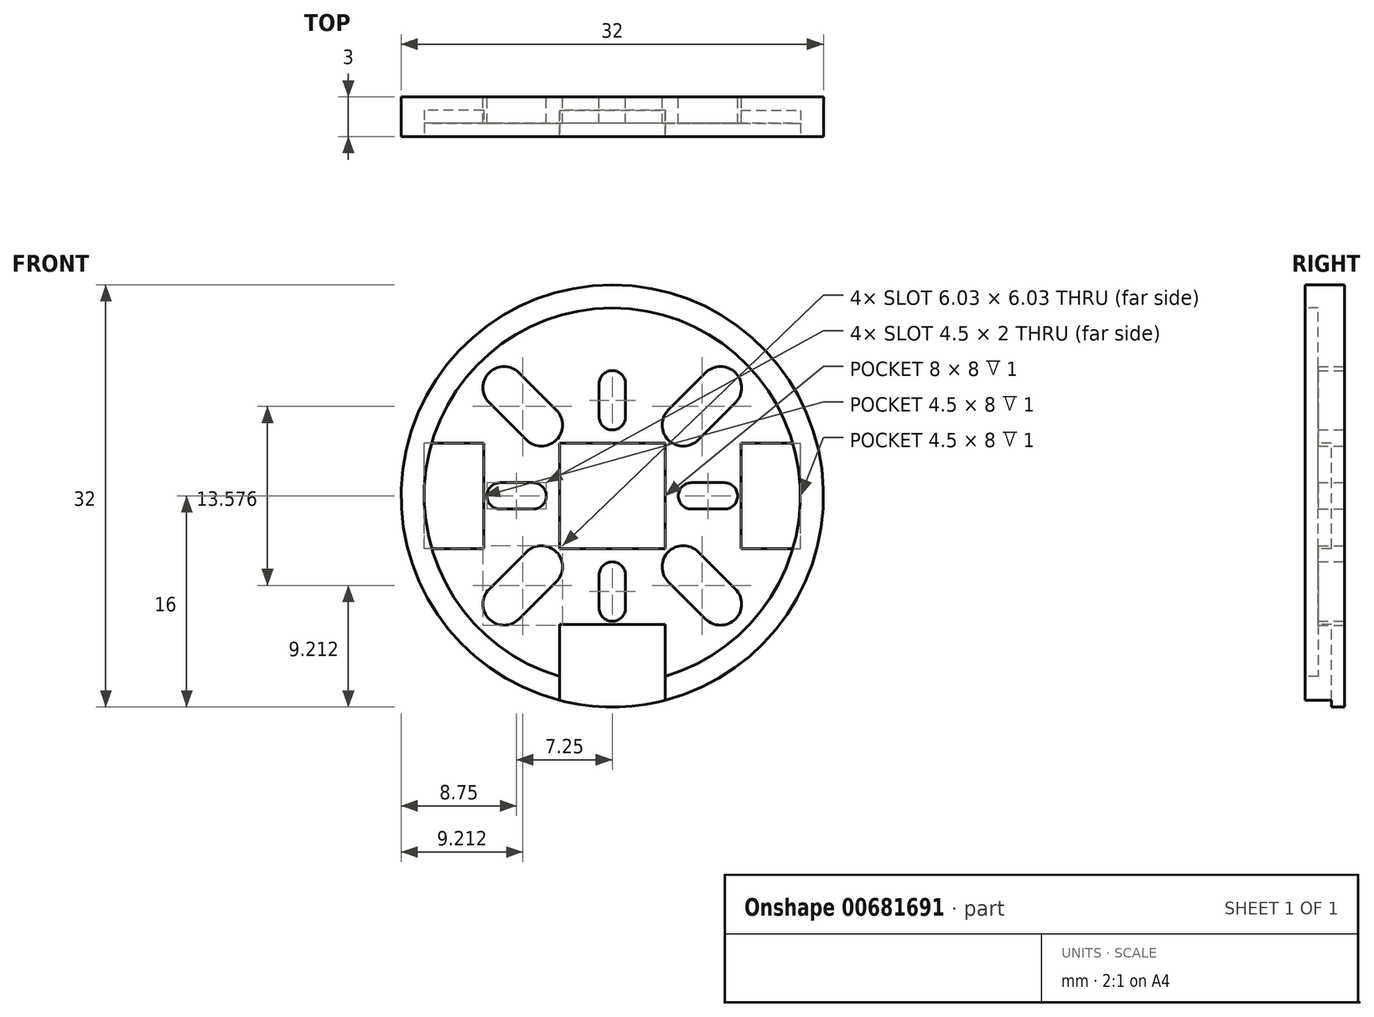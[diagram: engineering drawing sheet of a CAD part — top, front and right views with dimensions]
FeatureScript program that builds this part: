
annotation { "Feature Type Name" : "Feature", "Feature Type Description" : "" }
export const myFeature = defineFeature(function(context is Context, id is Id, definition is map)
    precondition{}
    {
        {
            var Q0;
            Q0=qCreatedBy(makeId("Front.planeOp"),FACE);
            var sketch = newSketch(context, id + "F0", { "sketchPlane" : qUnion([Q0])});
            skCircle(sketch, "E0", {"center": v(0, 0) * mm, "radius": 16 * mm});
            skSolve(sketch);
        }
        {
            var Q0;
            Q0 = qSketchRegion(id + "F0", true);
            extrude(context, id + "F1", {"entities" : qUnion([Q0]), "depth" : 3 * mm, "offsetDistance" : 25 * mm});
        }
        {
            var Q0;
            Q0=makeQuery(id+"F1.opExtrude","CAP_FACE",FACE,{"disambiguationData":[OSD([sQuery(id+"F0.wireOp",EDGE,"E0")])],"isStart":false});
            var sketch = newSketch(context, id + "F2", { "sketchPlane" : qUnion([Q0])});
            skArc(sketch, "E1", {"start": v(4, -13.68) * mm, "mid": v(0, 14.25) * mm, "end": v(-4, -13.68) * mm});
            skLineSegment(sketch, "E2.bottom", {"start": v(4, -16.68) * mm, "end": v(-4, -16.68) * mm});
            skLineSegment(sketch, "E2.left", {"start": v(4, -16.68) * mm, "end": v(4, -13.68) * mm});
            skLineSegment(sketch, "E2.right", {"start": v(-4, -16.68) * mm, "end": v(-4, -13.68) * mm});
            skPoint(sketch, "E2.middle", {"position": v(0, -15.18) * mm});
            skSolve(sketch);
        }
        {
            var Q0;
            Q0 = qSketchRegion(id + "F2", true);
            extrude(context, id + "F3", {"entities" : qUnion([Q0]), "operationType" : NewBodyOperationType.REMOVE, "oppositeDirection" : true, "depth" : 1 * mm, "offsetDistance" : 25 * mm});
        }
        {
            var Q0;
            Q0=makeQuery(id+"F3.boolean.opBoolean","COPY",FACE,{"derivedFrom":makeQuery(id+"F3.opExtrude","CAP_FACE",FACE,{"disambiguationData":[OSD([sQuery(id+"F2.wireOp",EDGE,"E1"),sQuery(id+"F2.wireOp",EDGE,"E2.bottom"),sQuery(id+"F2.wireOp",EDGE,"E2.left"),sQuery(id+"F2.wireOp",EDGE,"E2.right")])],"isStart":false})});
            var sketch = newSketch(context, id + "F4", { "sketchPlane" : qUnion([Q0])});
            skLineSegment(sketch, "E3.bottom", {"start": v(4, -4) * mm, "end": v(-4, -4) * mm});
            skLineSegment(sketch, "E3.top", {"start": v(4, 4) * mm, "end": v(-4, 4) * mm});
            skLineSegment(sketch, "E3.left", {"start": v(4, -4) * mm, "end": v(4, 4) * mm});
            skLineSegment(sketch, "E3.right", {"start": v(-4, -4) * mm, "end": v(-4, 4) * mm});
            skPoint(sketch, "E3.middle", {"position": v(0, 0) * mm});
            skLineSegment(sketch, "E4.bottom", {"start": v(-9.75, -4) * mm, "end": v(-14.25, -4) * mm});
            skLineSegment(sketch, "E4.top", {"start": v(-9.75, 4) * mm, "end": v(-14.25, 4) * mm});
            skLineSegment(sketch, "E4.left", {"start": v(-9.75, -4) * mm, "end": v(-9.75, 4) * mm});
            skLineSegment(sketch, "E4.right", {"start": v(-14.25, -4) * mm, "end": v(-14.25, 4) * mm});
            skPoint(sketch, "E4.middle", {"position": v(-12, 0) * mm});
            skLineSegment(sketch, "E5.MirrorCS", {"start": v(14.25, -4) * mm, "end": v(14.25, 4) * mm});
            skLineSegment(sketch, "E6.MirrorCS", {"start": v(9.75, -4) * mm, "end": v(14.25, -4) * mm});
            skLineSegment(sketch, "E7.MirrorCS", {"start": v(9.75, 4) * mm, "end": v(14.25, 4) * mm});
            skLineSegment(sketch, "E8.MirrorCS", {"start": v(9.75, -4) * mm, "end": v(9.75, 4) * mm});
            skLineSegment(sketch, "E9.1.0", {"start": v(4, -9.75) * mm, "end": v(-4, -9.75) * mm});
            skLineSegment(sketch, "E9.1.1", {"start": v(-4, -9.75) * mm, "end": v(-4, -14.25) * mm});
            skLineSegment(sketch, "E9.1.2", {"start": v(4, -14.25) * mm, "end": v(-4, -14.25) * mm, "construction": true});
            skLineSegment(sketch, "E9.1.3", {"start": v(4, -9.75) * mm, "end": v(4, -14.25) * mm});
            skLineSegment(sketch, "E9.anchor1", {"start": v(0, 0) * mm, "end": v(-14.25, -4) * mm, "construction": true});
            skLineSegment(sketch, "E9.anchor2", {"start": v(0, 0) * mm, "end": v(4, -14.25) * mm, "construction": true});
            skArc(sketch, "E10.0", {"start": v(-4, -15.5) * mm, "mid": v(0, -16) * mm, "end": v(4, -15.5) * mm});
            skLineSegment(sketch, "E11.0", {"start": v(-4, -15.5) * mm, "end": v(-4, -13.68) * mm});
            skLineSegment(sketch, "E12.0", {"start": v(4, -15.5) * mm, "end": v(4, -13.68) * mm});
            skSolve(sketch);
        }
        {
            var Q0;
            Q0 = qSketchRegion(id + "F4", true);
            extrude(context, id + "F5", {"entities" : qUnion([Q0]), "operationType" : NewBodyOperationType.REMOVE, "oppositeDirection" : true, "depth" : 1 * mm, "offsetDistance" : 25 * mm});
        }
        {
            var Q0;
            Q0=makeQuery(id+"F1.opExtrude","CAP_FACE",FACE,{"disambiguationData":[OSD([sQuery(id+"F0.wireOp",EDGE,"E0")])],"isStart":true});
            var sketch = newSketch(context, id + "F6", { "sketchPlane" : qUnion([Q0])});
            skArc(sketch, "E13", {"start": v(1, 8.5) * mm, "mid": v(0, 9.5) * mm, "end": v(-1, 8.5) * mm});
            skArc(sketch, "E14", {"start": v(-1, 6) * mm, "mid": v(0, 5) * mm, "end": v(1, 6) * mm});
            skLineSegment(sketch, "E15", {"start": v(-1, 8.5) * mm, "end": v(-1, 6) * mm});
            skLineSegment(sketch, "E16", {"start": v(1, 6) * mm, "end": v(1, 8.5) * mm});
            skLineSegment(sketch, "E17.1.0", {"start": v(-8.5, -1) * mm, "end": v(-6, -1) * mm});
            skLineSegment(sketch, "E17.1.1", {"start": v(-6, 1) * mm, "end": v(-8.5, 1) * mm});
            skArc(sketch, "E17.1.2", {"start": v(-6, -1) * mm, "mid": v(-5, 0) * mm, "end": v(-6, 1) * mm});
            skArc(sketch, "E17.1.3", {"start": v(-8.5, 1) * mm, "mid": v(-9.5, 0) * mm, "end": v(-8.5, -1) * mm});
            skLineSegment(sketch, "E17.2.0", {"start": v(1, -8.5) * mm, "end": v(1, -6) * mm});
            skLineSegment(sketch, "E17.2.1", {"start": v(-1, -6) * mm, "end": v(-1, -8.5) * mm});
            skArc(sketch, "E17.2.2", {"start": v(1, -6) * mm, "mid": v(0, -5) * mm, "end": v(-1, -6) * mm});
            skArc(sketch, "E17.2.3", {"start": v(-1, -8.5) * mm, "mid": v(0, -9.5) * mm, "end": v(1, -8.5) * mm});
            skLineSegment(sketch, "E17.3.0", {"start": v(8.5, 1) * mm, "end": v(6, 1) * mm});
            skLineSegment(sketch, "E17.3.1", {"start": v(6, -1) * mm, "end": v(8.5, -1) * mm});
            skArc(sketch, "E17.3.2", {"start": v(6, 1) * mm, "mid": v(5, 0) * mm, "end": v(6, -1) * mm});
            skArc(sketch, "E17.3.3", {"start": v(8.5, -1) * mm, "mid": v(9.5, 0) * mm, "end": v(8.5, 1) * mm});
            skPoint(sketch, "E17.center", {"position": v(0, 0) * mm});
            skSolve(sketch);
        }
        {
            var Q0;
            Q0 = qSketchRegion(id + "F6", true);
            extrude(context, id + "F7", {"entities" : qUnion([Q0]), "operationType" : NewBodyOperationType.REMOVE, "endBound" : BoundingType.THROUGH_ALL, "oppositeDirection" : true, "depth" : 25 * mm, "offsetDistance" : 25 * mm});
        }
        {
            var Q0;
            Q0=makeQuery(id+"F1.opExtrude","CAP_FACE",FACE,{"disambiguationData":[OSD([sQuery(id+"F0.wireOp",EDGE,"E0")])],"isStart":true});
            var sketch = newSketch(context, id + "F8", { "sketchPlane" : qUnion([Q0])});
            skLineSegment(sketch, "E18", {"start": v(0, 0) * mm, "end": v(-10.7, -10.7) * mm, "construction": true});
            skCircle(sketch, "E19", {"center": v(-8.2, -8.2) * mm, "radius": 1.6 * mm});
            skCircle(sketch, "E20", {"center": v(-5.37, -5.37) * mm, "radius": 1.6 * mm});
            skLineSegment(sketch, "E21", {"start": v(-6.5, -4.24) * mm, "end": v(-9.33, -7.07) * mm});
            skLineSegment(sketch, "E22", {"start": v(-4.24, -6.5) * mm, "end": v(-7.07, -9.33) * mm});
            skLineSegment(sketch, "E23.1.0", {"start": v(0, 0) * mm, "end": v(10.7, -10.7) * mm, "construction": true});
            skLineSegment(sketch, "E23.1.1", {"start": v(6.5, -4.24) * mm, "end": v(9.33, -7.07) * mm});
            skCircle(sketch, "E23.1.2", {"center": v(8.2, -8.2) * mm, "radius": 1.6 * mm});
            skLineSegment(sketch, "E23.1.3", {"start": v(4.24, -6.5) * mm, "end": v(7.07, -9.33) * mm});
            skCircle(sketch, "E23.1.4", {"center": v(5.37, -5.37) * mm, "radius": 1.6 * mm});
            skLineSegment(sketch, "E23.2.0", {"start": v(0, 0) * mm, "end": v(10.7, 10.7) * mm, "construction": true});
            skLineSegment(sketch, "E23.2.1", {"start": v(4.24, 6.5) * mm, "end": v(7.07, 9.33) * mm});
            skCircle(sketch, "E23.2.2", {"center": v(8.2, 8.2) * mm, "radius": 1.6 * mm});
            skLineSegment(sketch, "E23.2.3", {"start": v(6.5, 4.24) * mm, "end": v(9.33, 7.07) * mm});
            skCircle(sketch, "E23.2.4", {"center": v(5.37, 5.37) * mm, "radius": 1.6 * mm});
            skLineSegment(sketch, "E23.3.0", {"start": v(0, 0) * mm, "end": v(-10.7, 10.7) * mm, "construction": true});
            skLineSegment(sketch, "E23.3.1", {"start": v(-6.5, 4.24) * mm, "end": v(-9.33, 7.07) * mm});
            skCircle(sketch, "E23.3.2", {"center": v(-8.2, 8.2) * mm, "radius": 1.6 * mm});
            skLineSegment(sketch, "E23.3.3", {"start": v(-4.24, 6.5) * mm, "end": v(-7.07, 9.33) * mm});
            skCircle(sketch, "E23.3.4", {"center": v(-5.37, 5.37) * mm, "radius": 1.6 * mm});
            skPoint(sketch, "E23.center", {"position": v(0, 0) * mm});
            skSolve(sketch);
        }
        {
            var Q0;
            Q0 = qSketchRegion(id + "F8", true);
            extrude(context, id + "F9", {"entities" : qUnion([Q0]), "operationType" : NewBodyOperationType.REMOVE, "endBound" : BoundingType.THROUGH_ALL, "oppositeDirection" : true, "depth" : 25 * mm, "offsetDistance" : 25 * mm});
        }
    });
